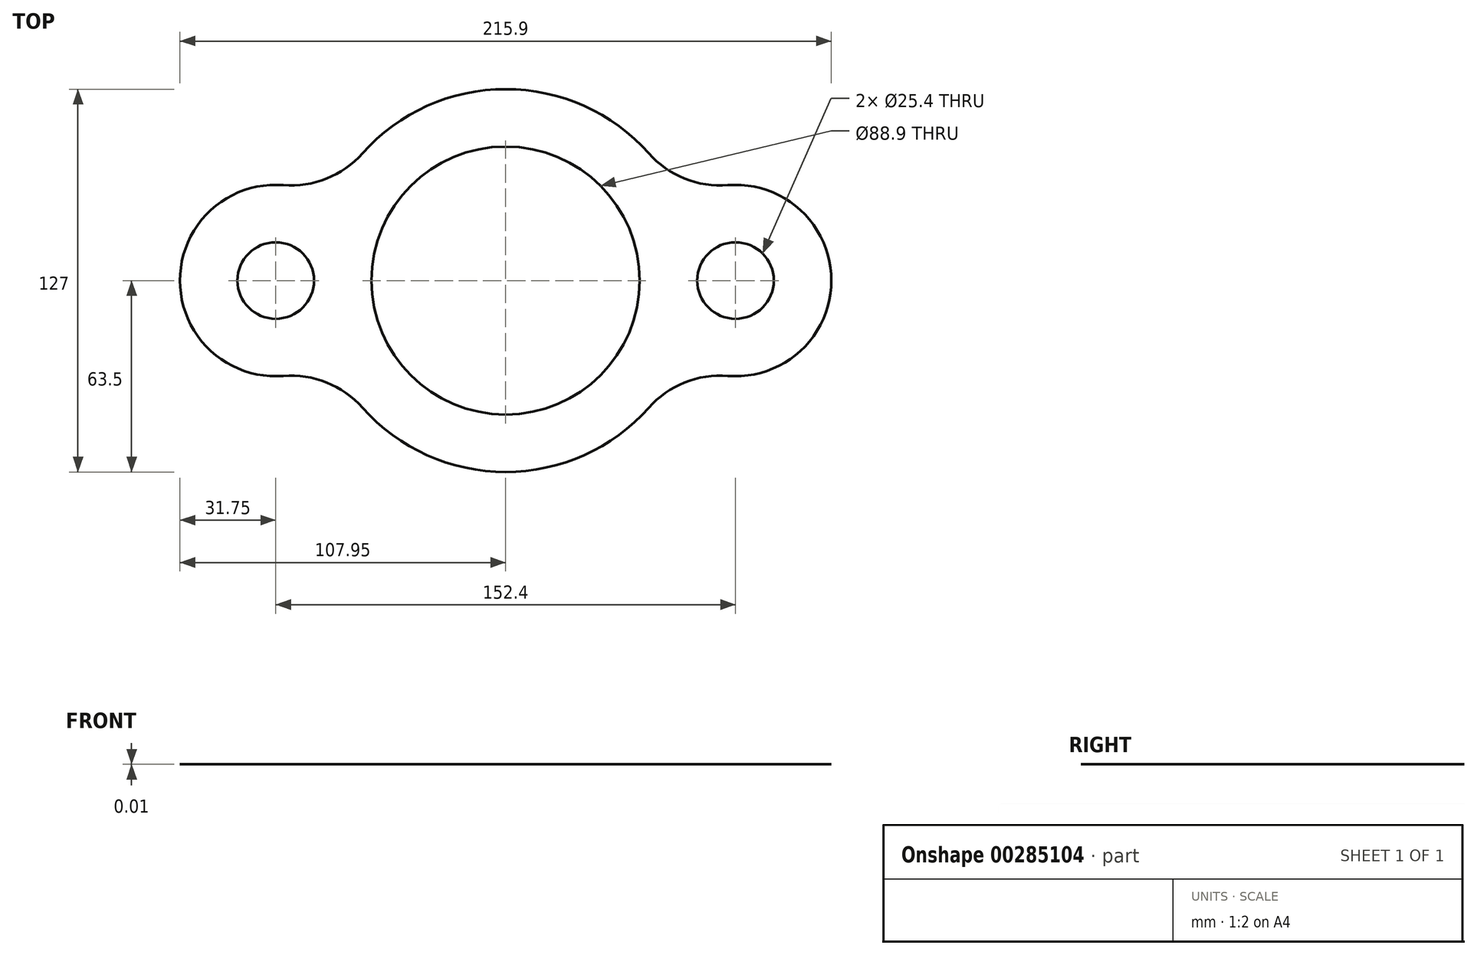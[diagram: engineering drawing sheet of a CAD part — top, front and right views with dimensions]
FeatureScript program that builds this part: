
annotation { "Feature Type Name" : "Feature", "Feature Type Description" : "" }
export const myFeature = defineFeature(function(context is Context, id is Id, definition is map)
    precondition{}
    {
        {
            var Q0;
            Q0=qCreatedBy(makeId("Top.planeOp"),FACE);
            var sketch = newSketch(context, id + "F0", { "sketchPlane" : qUnion([Q0])});
            skCircle(sketch, "E0", {"center": v(0, 0) * mm, "radius": 44.45 * mm});
            skLineSegment(sketch, "E1", {"start": v(0, 0) * mm, "end": v(0, 44.45) * mm});
            skLineSegment(sketch, "E2", {"start": v(0, 0) * mm, "end": v(0, -44.45) * mm});
            skArc(sketch, "E3", {"start": v(-47.45, -42.2) * mm, "mid": v(0, -63.5) * mm, "end": v(47.45, -42.2) * mm});
            skCircle(sketch, "E4", {"center": v(-76.2, 0) * mm, "radius": 12.7 * mm});
            skCircle(sketch, "E5", {"center": v(76.2, 0) * mm, "radius": 12.7 * mm});
            skArc(sketch, "E6", {"start": v(-73.69, 31.65) * mm, "mid": v(-107.95, 0) * mm, "end": v(-73.69, -31.65) * mm});
            skArc(sketch, "E7", {"start": v(73.69, -31.65) * mm, "mid": v(107.95, 0) * mm, "end": v(73.69, 31.65) * mm});
            skArc(sketch, "E8.trimOffspring", {"start": v(47.45, 42.2) * mm, "mid": v(0, 63.5) * mm, "end": v(-47.45, 42.2) * mm});
            skPoint(sketch, "E9.visualSharp", {"position": v(-57.94, 25.98) * mm});
            skArc(sketch, "E9.filletArc", {"start": v(-73.69, 31.65) * mm, "mid": v(-59.33, 33.84) * mm, "end": v(-47.45, 42.2) * mm});
            skPoint(sketch, "E10.visualSharp", {"position": v(-57.94, -25.98) * mm});
            skArc(sketch, "E10.filletArc", {"start": v(-47.45, -42.2) * mm, "mid": v(-59.33, -33.84) * mm, "end": v(-73.69, -31.65) * mm});
            skPoint(sketch, "E11.visualSharp", {"position": v(57.94, 25.98) * mm});
            skArc(sketch, "E11.filletArc", {"start": v(47.45, 42.2) * mm, "mid": v(59.33, 33.84) * mm, "end": v(73.69, 31.65) * mm});
            skPoint(sketch, "E12.visualSharp", {"position": v(57.94, -25.98) * mm});
            skArc(sketch, "E12.filletArc", {"start": v(73.69, -31.65) * mm, "mid": v(59.33, -33.84) * mm, "end": v(47.45, -42.2) * mm});
            skSolve(sketch);
        }
        {
            var Q0;
            Q0=makeQuery(id+"F0.imprint","IMPRINT",FACE,{"disambiguationData":[TD([[makeQuery(id+"F0.imprint","IMPRINT",EDGE,{"derivedFrom":sQuery(id+"F0.wireOp",EDGE,"E3")}),1.0]])]});
            extrude(context, id + "F1", {"entities" : qUnion([Q0]), "depth" : 1 / 101.6 * mm});
        }
    });
